# Revit family: TYCO-FPP-Zettler-MIO800 Multi inputoutput module
name_source: partatom
category: Electrical Fixtures
revit_build: Autodesk Revit 2014 (Build: 20130308_1515(x64)
units: mm (PartAtom-declared; Revit-internal decimal feet)

## types (1)
- TYCO-FPP-Zettler-MIO800 Multi inputoutput module
    Ambient Temperature = –25°C to +70°C
    Description = The MIO800 Addressable Multi-Input/Output Module has
three inputs and two outputs from latching relays that
communicates with compatible MX Control and Indicating
Equipment (CIE).
    Input Alarm Resistor = 150 Ohm
    Input EOL = 330 Ohm
    LED = RED
    Length = 72 mm
    Loop Voltage = 20V to 40Vdc
    Manufacturer = Tyco
    Max. MIO800 per Loop2 = 250
250
    Maximum Circuit Resistance = 40 Ohm
40 Ohm
    Model = Zettler-555.800.065
    PCB = PCB
    Quiescent Current = 480μA
480μA
    RS = RS
    Relative Humidity = 10% to 95%
    STT = BLACKK
    Storage Temperature = –40°C to +80°C
    Type Comments = Three configurable inputs and two relay
outputs from latching relays
    URL = https://www.tycosafetyproducts-anz.com
    Width = 110 mm

## geometry (parser evidence)
native form markers: Sweep x1
no freeform markers — native parametric forms only
